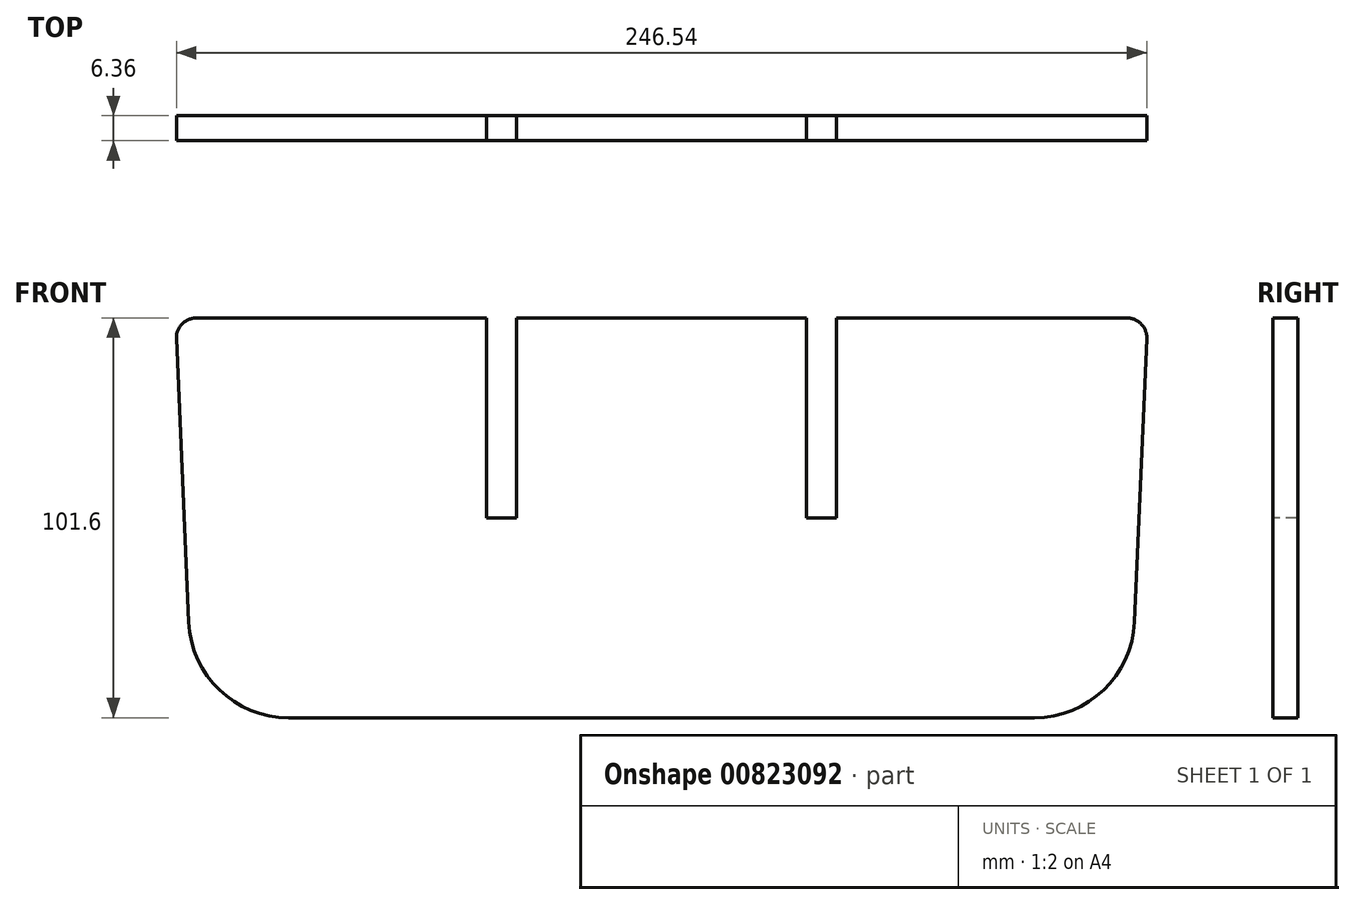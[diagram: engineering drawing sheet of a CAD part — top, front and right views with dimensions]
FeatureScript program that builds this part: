
annotation { "Feature Type Name" : "Feature", "Feature Type Description" : "" }
export const myFeature = defineFeature(function(context is Context, id is Id, definition is map)
    precondition{}
    {
        {
            var Q0;
            Q0=qCreatedBy(makeId("Front.planeOp"),FACE);
            var sketch = newSketch(context, id + "F0", { "sketchPlane" : qUnion([Q0])});
            skLineSegment(sketch, "E0", {"start": v(-123.5, 101.6) * mm, "end": v(-119.06, 0) * mm});
            skLineSegment(sketch, "E1", {"start": v(-119.06, 0) * mm, "end": v(119.06, 0) * mm});
            skLineSegment(sketch, "E2", {"start": v(119.06, 0) * mm, "end": v(123.5, 101.6) * mm});
            skLineSegment(sketch, "E3", {"start": v(123.5, 101.6) * mm, "end": v(-123.5, 101.6) * mm});
            skSolve(sketch);
        }
        {
            var Q0;
            Q0=qSketchRegion(id+"F0",true);
            extrude(context, id + "F1", {"entities" : qUnion([Q0]), "endBound" : BoundingType.SYMMETRIC, "depth" : 6.35 * mm, "offsetDistance" : 25.4 * mm});
        }
        {
            var Q0;
            Q0=qCreatedBy(makeId("Front.planeOp"),FACE);
            var sketch = newSketch(context, id + "F2", { "sketchPlane" : qUnion([Q0])});
            skLineSegment(sketch, "E4", {"start": v(-40.64, 94.02) * mm, "end": v(-40.64, -20.45) * mm, "construction": true});
            skLineSegment(sketch, "E5.bottom", {"start": v(-36.83, 50.8) * mm, "end": v(-44.45, 50.8) * mm});
            skLineSegment(sketch, "E5.top", {"start": v(-36.83, 101.6) * mm, "end": v(-44.45, 101.6) * mm});
            skLineSegment(sketch, "E5.left", {"start": v(-36.83, 50.8) * mm, "end": v(-36.83, 101.6) * mm});
            skLineSegment(sketch, "E5.right", {"start": v(-44.45, 50.8) * mm, "end": v(-44.45, 101.6) * mm});
            skLineSegment(sketch, "E6.MirrorCS", {"start": v(36.83, 50.8) * mm, "end": v(44.45, 50.8) * mm});
            skLineSegment(sketch, "E7.MirrorCS", {"start": v(36.83, 101.6) * mm, "end": v(44.45, 101.6) * mm});
            skLineSegment(sketch, "E8.MirrorCS", {"start": v(36.83, 50.8) * mm, "end": v(36.83, 101.6) * mm});
            skLineSegment(sketch, "E9.MirrorCS", {"start": v(44.45, 50.8) * mm, "end": v(44.45, 101.6) * mm});
            skSolve(sketch);
        }
        {
            var Q0;
            Q0=qSketchRegion(id+"F2",true);
            extrude(context, id + "F3", {"entities" : qUnion([Q0]), "operationType" : NewBodyOperationType.REMOVE, "endBound" : BoundingType.SYMMETRIC, "oppositeDirection" : true, "depth" : 25.4 * mm, "offsetDistance" : 25.4 * mm});
        }
        {
            var Q0;
            Q0=makeQuery(id+"F1.opExtrude","SWEPT_EDGE",EDGE,{"disambiguationData":[OSD([sQuery(id+"F0.wireOp",EDGE,"E0"),sQuery(id+"F0.wireOp",EDGE,"E1")])]});
            var Q1;
            Q1=makeQuery(id+"F1.opExtrude","SWEPT_EDGE",EDGE,{"disambiguationData":[OSD([sQuery(id+"F0.wireOp",EDGE,"E1"),sQuery(id+"F0.wireOp",EDGE,"E2")])]});
            fillet(context, id + "F4", {"entities" : qUnion([Q0, Q1]), "radius" : 25.4 * mm, "tangentPropagation" : true, "allowEdgeOverflow" : false});
        }
        {
            var Q0;
            Q0=makeQuery(id+"F1.opExtrude","SWEPT_EDGE",EDGE,{"disambiguationData":[OSD([sQuery(id+"F0.wireOp",EDGE,"E0"),sQuery(id+"F0.wireOp",EDGE,"E3")])]});
            var Q1;
            Q1=makeQuery(id+"F1.opExtrude","SWEPT_EDGE",EDGE,{"disambiguationData":[OSD([sQuery(id+"F0.wireOp",EDGE,"E2"),sQuery(id+"F0.wireOp",EDGE,"E3")])]});
            fillet(context, id + "F5", {"entities" : qUnion([Q0, Q1]), "radius" : 5.08 * mm, "tangentPropagation" : true, "allowEdgeOverflow" : false});
        }
    });
